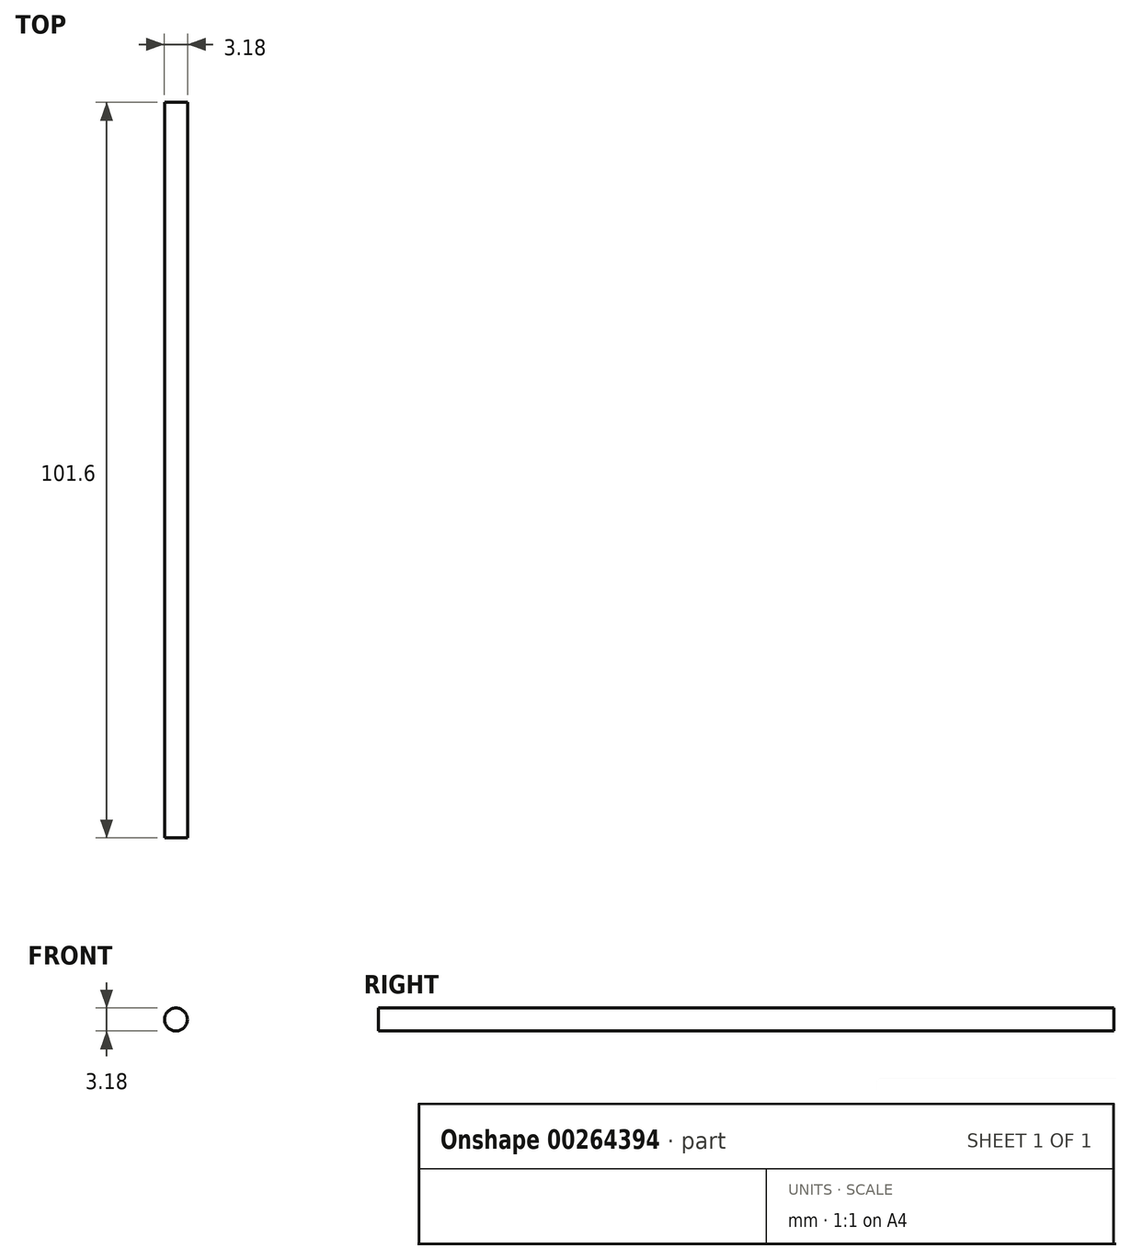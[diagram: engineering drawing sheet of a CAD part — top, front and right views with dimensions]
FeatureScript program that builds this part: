
annotation { "Feature Type Name" : "Feature", "Feature Type Description" : "" }
export const myFeature = defineFeature(function(context is Context, id is Id, definition is map)
    precondition{}
    {
        {
            var Q0;
            Q0=qCreatedBy(makeId("Front.planeOp"),FACE);
            var sketch = newSketch(context, id + "F0", { "sketchPlane" : qUnion([Q0])});
            skCircle(sketch, "E0", {"center": v(0, 0) * mm, "radius": 1.59 * mm});
            skSolve(sketch);
        }
        {
            var Q0;
            Q0 = qSketchRegion(id + "F0", true);
            extrude(context, id + "F1", {"entities" : qUnion([Q0]), "depth" : 101.6 * mm});
        }
    });
